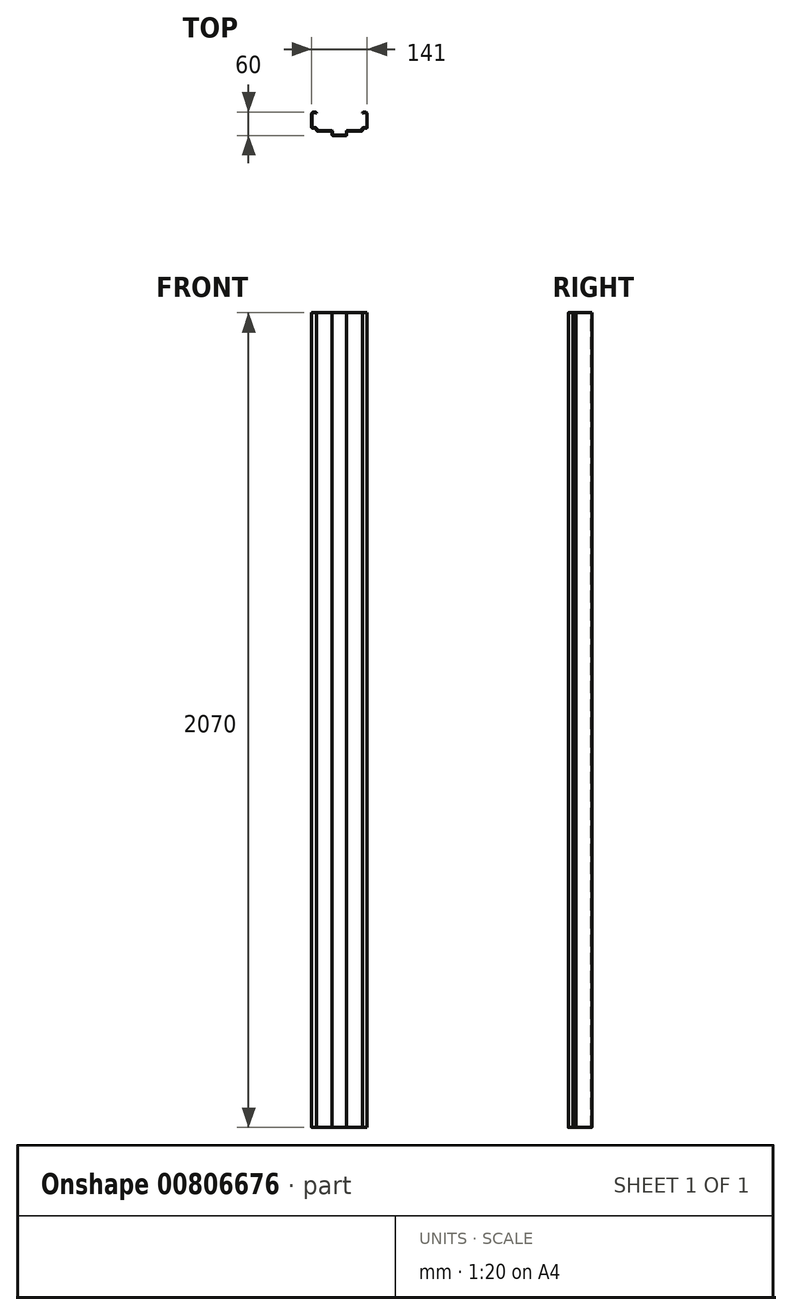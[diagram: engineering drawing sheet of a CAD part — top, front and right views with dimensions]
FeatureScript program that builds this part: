
annotation { "Feature Type Name" : "Feature", "Feature Type Description" : "" }
export const myFeature = defineFeature(function(context is Context, id is Id, definition is map)
    precondition{}
    {
        {
            var Q0;
            Q0=qCreatedBy(makeId("Top.planeOp"),FACE);
            var sketch = newSketch(context, id + "F0", { "sketchPlane" : qUnion([Q0])});
            skLineSegment(sketch, "E0", {"start": v(0, 0) * mm, "end": v(-18.5, 0) * mm});
            skLineSegment(sketch, "E1", {"start": v(-18.5, 0) * mm, "end": v(-18.5, 12) * mm});
            skLineSegment(sketch, "E2", {"start": v(-18.5, 12) * mm, "end": v(-58.5, 12) * mm});
            skLineSegment(sketch, "E3", {"start": v(-58.5, 12) * mm, "end": v(-58.5, 19) * mm});
            skLineSegment(sketch, "E4", {"start": v(-58.5, 19) * mm, "end": v(-70.5, 19) * mm});
            skLineSegment(sketch, "E5", {"start": v(-70.5, 19) * mm, "end": v(-70.5, 60) * mm});
            skLineSegment(sketch, "E6", {"start": v(-70.5, 60) * mm, "end": v(-58.5, 60) * mm});
            skLineSegment(sketch, "E7.MirrorCS", {"start": v(0, 0) * mm, "end": v(18.5, 0) * mm});
            skLineSegment(sketch, "E8.MirrorCS", {"start": v(18.5, 0) * mm, "end": v(18.5, 12) * mm});
            skLineSegment(sketch, "E9.MirrorCS", {"start": v(18.5, 12) * mm, "end": v(58.5, 12) * mm});
            skLineSegment(sketch, "E10.MirrorCS", {"start": v(58.5, 12) * mm, "end": v(58.5, 19) * mm});
            skLineSegment(sketch, "E11.MirrorCS", {"start": v(58.5, 19) * mm, "end": v(70.5, 19) * mm});
            skLineSegment(sketch, "E12.MirrorCS", {"start": v(70.5, 19) * mm, "end": v(70.5, 60) * mm});
            skLineSegment(sketch, "E13.MirrorCS", {"start": v(70.5, 60) * mm, "end": v(58.5, 60) * mm});
            skLineSegment(sketch, "E14", {"start": v(-58.5, 60) * mm, "end": v(-58.5, 57) * mm});
            skLineSegment(sketch, "E15.MirrorCS", {"start": v(58.5, 60) * mm, "end": v(58.5, 57) * mm});
            skLineSegment(sketch, "E16.0", {"start": v(-69.5, 20) * mm, "end": v(-69.5, 59) * mm});
            skLineSegment(sketch, "E16.1", {"start": v(-57.5, 20) * mm, "end": v(-69.5, 20) * mm});
            skLineSegment(sketch, "E16.2", {"start": v(0, 1) * mm, "end": v(-17.5, 1) * mm});
            skLineSegment(sketch, "E16.3", {"start": v(-17.5, 1) * mm, "end": v(-17.5, 13) * mm});
            skLineSegment(sketch, "E16.4", {"start": v(-17.5, 13) * mm, "end": v(-57.5, 13) * mm});
            skLineSegment(sketch, "E16.5", {"start": v(-57.5, 13) * mm, "end": v(-57.5, 20) * mm});
            skLineSegment(sketch, "E17", {"start": v(-69.5, 59) * mm, "end": v(-59.5, 59) * mm});
            skLineSegment(sketch, "E18", {"start": v(-59.5, 59) * mm, "end": v(-59.5, 57) * mm});
            skLineSegment(sketch, "E19", {"start": v(-59.5, 57) * mm, "end": v(-58.5, 57) * mm});
            skLineSegment(sketch, "E20.MirrorCS", {"start": v(0, 1) * mm, "end": v(17.5, 1) * mm});
            skLineSegment(sketch, "E21.MirrorCS", {"start": v(17.5, 1) * mm, "end": v(17.5, 13) * mm});
            skLineSegment(sketch, "E22.MirrorCS", {"start": v(17.5, 13) * mm, "end": v(57.5, 13) * mm});
            skLineSegment(sketch, "E23.MirrorCS", {"start": v(57.5, 13) * mm, "end": v(57.5, 20) * mm});
            skLineSegment(sketch, "E24.MirrorCS", {"start": v(57.5, 20) * mm, "end": v(69.5, 20) * mm});
            skLineSegment(sketch, "E25.MirrorCS", {"start": v(69.5, 20) * mm, "end": v(69.5, 59) * mm});
            skLineSegment(sketch, "E26.MirrorCS", {"start": v(69.5, 59) * mm, "end": v(59.5, 59) * mm});
            skLineSegment(sketch, "E27.MirrorCS", {"start": v(59.5, 59) * mm, "end": v(59.5, 57) * mm});
            skLineSegment(sketch, "E28.MirrorCS", {"start": v(59.5, 57) * mm, "end": v(58.5, 57) * mm});
            skSolve(sketch);
        }
        {
            var Q0;
            Q0=makeQuery(id+"F0.imprint","IMPRINT",FACE,{"disambiguationData":[TD([[makeQuery(id+"F0.imprint","IMPRINT",EDGE,{"derivedFrom":sQuery(id+"F0.wireOp",EDGE,"E0")}),-1.0]])]});
            extrude(context, id + "F1", {"entities" : qUnion([Q0]), "depth" : 2070 * mm, "offsetDistance" : 25 * mm});
        }
        {
            var Q0;
            Q0=makeQuery(id+"F1.opExtrude","SWEPT_EDGE",EDGE,{"disambiguationData":[OSD([sQuery(id+"F0.wireOp",EDGE,"E24.MirrorCS"),sQuery(id+"F0.wireOp",EDGE,"E25.MirrorCS")])]});
            var Q1;
            Q1=makeQuery(id+"F1.opExtrude","SWEPT_EDGE",EDGE,{"disambiguationData":[OSD([sQuery(id+"F0.wireOp",EDGE,"E23.MirrorCS"),sQuery(id+"F0.wireOp",EDGE,"E24.MirrorCS")])]});
            var Q2;
            Q2=makeQuery(id+"F1.opExtrude","SWEPT_EDGE",EDGE,{"disambiguationData":[OSD([sQuery(id+"F0.wireOp",EDGE,"E22.MirrorCS"),sQuery(id+"F0.wireOp",EDGE,"E23.MirrorCS")])]});
            var Q3;
            Q3=makeQuery(id+"F1.opExtrude","SWEPT_EDGE",EDGE,{"disambiguationData":[OSD([sQuery(id+"F0.wireOp",EDGE,"E21.MirrorCS"),sQuery(id+"F0.wireOp",EDGE,"E22.MirrorCS")])]});
            var Q4;
            Q4=makeQuery(id+"F1.opExtrude","SWEPT_EDGE",EDGE,{"disambiguationData":[OSD([sQuery(id+"F0.wireOp",EDGE,"E20.MirrorCS"),sQuery(id+"F0.wireOp",EDGE,"E21.MirrorCS")])]});
            var Q5;
            Q5=makeQuery(id+"F1.opExtrude","SWEPT_EDGE",EDGE,{"disambiguationData":[OSD([sQuery(id+"F0.wireOp",EDGE,"E17"),sQuery(id+"F0.wireOp",EDGE,"E18")])]});
            var Q6;
            Q6=makeQuery(id+"F1.opExtrude","SWEPT_EDGE",EDGE,{"disambiguationData":[OSD([sQuery(id+"F0.wireOp",EDGE,"E16.3"),sQuery(id+"F0.wireOp",EDGE,"E16.4")])]});
            var Q7;
            Q7=makeQuery(id+"F1.opExtrude","SWEPT_EDGE",EDGE,{"disambiguationData":[OSD([sQuery(id+"F0.wireOp",EDGE,"E16.1"),sQuery(id+"F0.wireOp",EDGE,"E16.5")])]});
            var Q8;
            Q8=makeQuery(id+"F1.opExtrude","SWEPT_EDGE",EDGE,{"disambiguationData":[OSD([sQuery(id+"F0.wireOp",EDGE,"E6"),sQuery(id+"F0.wireOp",EDGE,"E14")])]});
            var Q9;
            Q9=makeQuery(id+"F1.opExtrude","SWEPT_EDGE",EDGE,{"disambiguationData":[OSD([sQuery(id+"F0.wireOp",EDGE,"E16.2"),sQuery(id+"F0.wireOp",EDGE,"E16.3")])]});
            var Q10;
            Q10=makeQuery(id+"F1.opExtrude","SWEPT_EDGE",EDGE,{"disambiguationData":[OSD([sQuery(id+"F0.wireOp",EDGE,"E16.4"),sQuery(id+"F0.wireOp",EDGE,"E16.5")])]});
            var Q11;
            Q11=makeQuery(id+"F1.opExtrude","SWEPT_EDGE",EDGE,{"disambiguationData":[OSD([sQuery(id+"F0.wireOp",EDGE,"E16.0"),sQuery(id+"F0.wireOp",EDGE,"E16.1")])]});
            var Q12;
            Q12=makeQuery(id+"F1.opExtrude","SWEPT_EDGE",EDGE,{"disambiguationData":[OSD([sQuery(id+"F0.wireOp",EDGE,"E26.MirrorCS"),sQuery(id+"F0.wireOp",EDGE,"E27.MirrorCS")])]});
            var Q13;
            Q13=makeQuery(id+"F1.opExtrude","SWEPT_EDGE",EDGE,{"disambiguationData":[OSD([sQuery(id+"F0.wireOp",EDGE,"E13.MirrorCS"),sQuery(id+"F0.wireOp",EDGE,"E15.MirrorCS")])]});
            var Q14;
            Q14=makeQuery(id+"F1.opExtrude","SWEPT_EDGE",EDGE,{"disambiguationData":[OSD([sQuery(id+"F0.wireOp",EDGE,"E11.MirrorCS"),sQuery(id+"F0.wireOp",EDGE,"E12.MirrorCS")])]});
            var Q15;
            Q15=makeQuery(id+"F1.opExtrude","SWEPT_EDGE",EDGE,{"disambiguationData":[OSD([sQuery(id+"F0.wireOp",EDGE,"E10.MirrorCS"),sQuery(id+"F0.wireOp",EDGE,"E11.MirrorCS")])]});
            var Q16;
            Q16=makeQuery(id+"F1.opExtrude","SWEPT_EDGE",EDGE,{"disambiguationData":[OSD([sQuery(id+"F0.wireOp",EDGE,"E9.MirrorCS"),sQuery(id+"F0.wireOp",EDGE,"E10.MirrorCS")])]});
            var Q17;
            Q17=makeQuery(id+"F1.opExtrude","SWEPT_EDGE",EDGE,{"disambiguationData":[OSD([sQuery(id+"F0.wireOp",EDGE,"E8.MirrorCS"),sQuery(id+"F0.wireOp",EDGE,"E9.MirrorCS")])]});
            var Q18;
            Q18=makeQuery(id+"F1.opExtrude","SWEPT_EDGE",EDGE,{"disambiguationData":[OSD([sQuery(id+"F0.wireOp",EDGE,"E7.MirrorCS"),sQuery(id+"F0.wireOp",EDGE,"E8.MirrorCS")])]});
            var Q19;
            Q19=makeQuery(id+"F1.opExtrude","SWEPT_EDGE",EDGE,{"disambiguationData":[OSD([sQuery(id+"F0.wireOp",EDGE,"E0"),sQuery(id+"F0.wireOp",EDGE,"E1")])]});
            var Q20;
            Q20=makeQuery(id+"F1.opExtrude","SWEPT_EDGE",EDGE,{"disambiguationData":[OSD([sQuery(id+"F0.wireOp",EDGE,"E1"),sQuery(id+"F0.wireOp",EDGE,"E2")])]});
            var Q21;
            Q21=makeQuery(id+"F1.opExtrude","SWEPT_EDGE",EDGE,{"disambiguationData":[OSD([sQuery(id+"F0.wireOp",EDGE,"E2"),sQuery(id+"F0.wireOp",EDGE,"E3")])]});
            var Q22;
            Q22=makeQuery(id+"F1.opExtrude","SWEPT_EDGE",EDGE,{"disambiguationData":[OSD([sQuery(id+"F0.wireOp",EDGE,"E3"),sQuery(id+"F0.wireOp",EDGE,"E4")])]});
            var Q23;
            Q23=makeQuery(id+"F1.opExtrude","SWEPT_EDGE",EDGE,{"disambiguationData":[OSD([sQuery(id+"F0.wireOp",EDGE,"E4"),sQuery(id+"F0.wireOp",EDGE,"E5")])]});
            fillet(context, id + "F2", {"entities" : qUnion([Q0, Q1, Q2, Q3, Q4, Q5, Q6, Q7, Q8, Q9, Q10, Q11, Q12, Q13, Q14, Q15, Q16, Q17, Q18, Q19, Q20, Q21, Q22, Q23]), "radius" : 3 * mm, "rho" : 0.5, "crossSection" : FilletCrossSection.CONIC, "allowEdgeOverflow" : false});
        }
        {
            var Q0;
            Q0=makeQuery(id+"F1.opExtrude","SWEPT_EDGE",EDGE,{"disambiguationData":[OSD([sQuery(id+"F0.wireOp",EDGE,"E5"),sQuery(id+"F0.wireOp",EDGE,"E6")])]});
            var Q1;
            Q1=makeQuery(id+"F1.opExtrude","SWEPT_EDGE",EDGE,{"disambiguationData":[OSD([sQuery(id+"F0.wireOp",EDGE,"E16.0"),sQuery(id+"F0.wireOp",EDGE,"E17")])]});
            var Q2;
            Q2=makeQuery(id+"F1.opExtrude","SWEPT_EDGE",EDGE,{"disambiguationData":[OSD([sQuery(id+"F0.wireOp",EDGE,"E12.MirrorCS"),sQuery(id+"F0.wireOp",EDGE,"E13.MirrorCS")])]});
            var Q3;
            Q3=makeQuery(id+"F1.opExtrude","SWEPT_EDGE",EDGE,{"disambiguationData":[OSD([sQuery(id+"F0.wireOp",EDGE,"E25.MirrorCS"),sQuery(id+"F0.wireOp",EDGE,"E26.MirrorCS")])]});
            fillet(context, id + "F3", {"entities" : qUnion([Q0, Q1, Q2, Q3]), "radius" : 5 * mm, "allowEdgeOverflow" : false});
        }
        {
            var Q0;
            Q0=makeQuery(id+"F1.opExtrude","SWEPT_FACE",FACE,{"disambiguationData":[OSD([sQuery(id+"F0.wireOp",EDGE,"E12.MirrorCS")])]});
            cPlane(context, id + "F4", {"entities" : qUnion([Q0]), "cplaneType" : CPlaneType.OFFSET, "offset" : 0 * mm, "width" : 150 * mm, "height" : 150 * mm});
        }
    });
